# Revit family: sh-1291-c
name_source: partatom
category: Lighting Fixtures
revit_build: Autodesk Revit 2017 (Build: 20160225_1515(x64)
units: mm (PartAtom-declared; Revit-internal decimal feet)

## family parameters
Always vertical = Yes
Cut with Voids When Loaded = No
Light Source = No
OmniClass Number = 23.80.70.00
OmniClass Title = Lighting
Part Type = Normal
Room Calculation Point = No
Round Connector Dimension = Use Diameter
Shared = No
Work Plane-Based = No

## types (3) — shared parameters
Body Material = Aluminium
Body color = Black
Cutting Diameter = 10.9 cm
Diameter = 11.9 cm
Flicker = FREE Flicker
Height = 10.7 cm
IP = IP66
Lamp = LED
Manufacturer = SHOA
Model = SH-1291-c
Protection Class = Class I
Type medule = Power Led
URL = https://www.shoaco.com
Voltage/Frequency = 230V-50HZ
color rendering index(CRI) = 80
consumption current = 0 A
instalation = inground
wattage. = 7 W
website = www.shoaco.com

## per-type parameters (varying)
| type | color temperature |
| SH-1291-c(Aluminium body-2000K-LED) | 2000K |
| SH-1291-c(Aluminium body-3000K-LED) | 3000K |
| SH-1291-c(Aluminium body-6500K-LED) | 6500K |

## geometry (parser evidence)
native form markers: Sweep x3
no freeform markers — native parametric forms only
